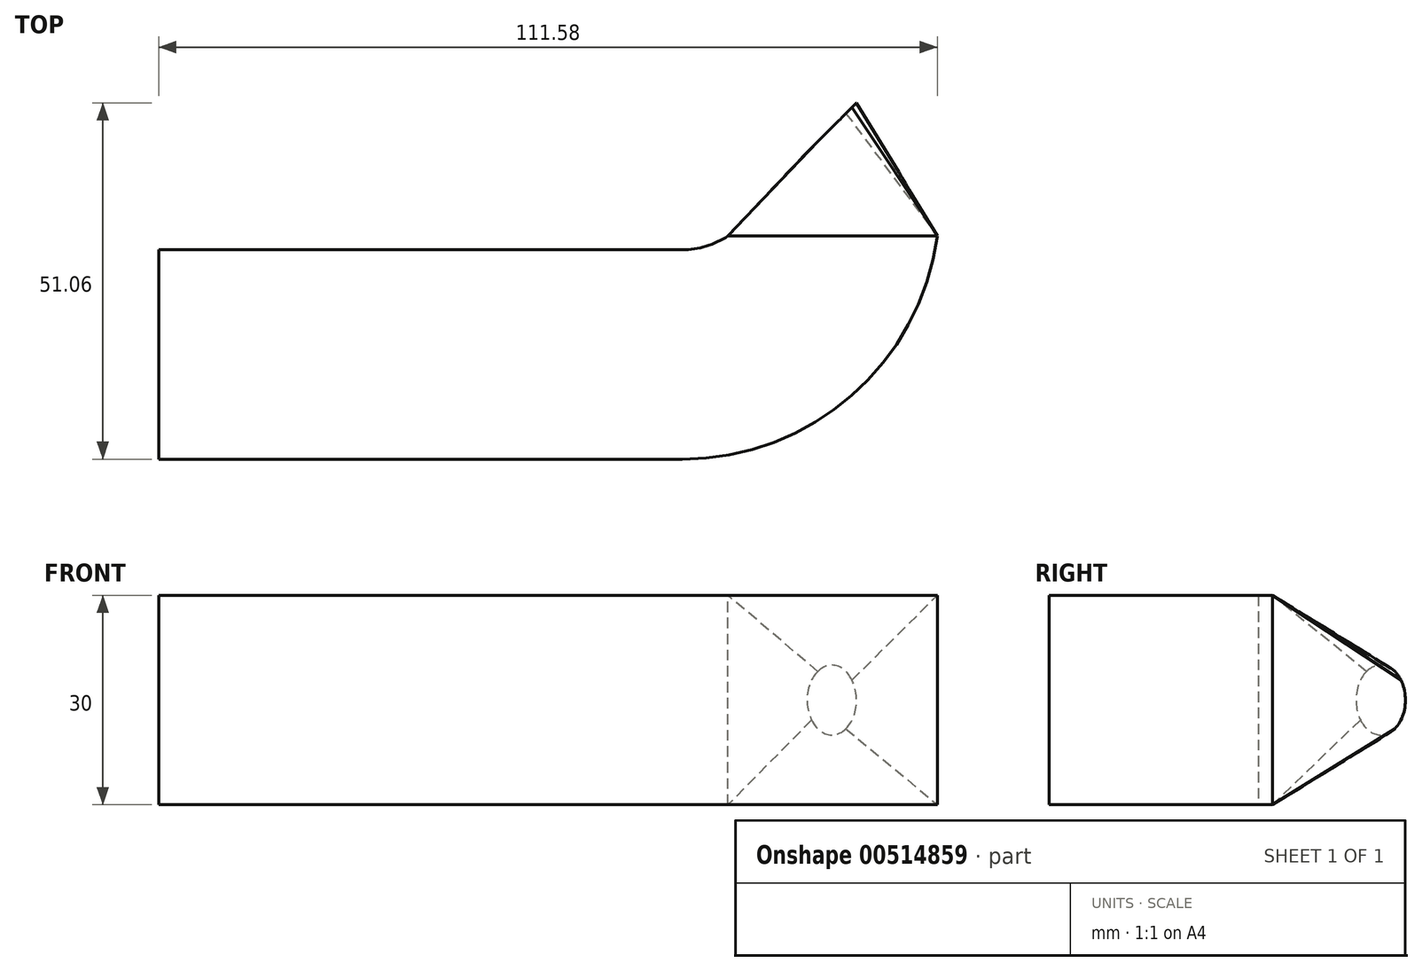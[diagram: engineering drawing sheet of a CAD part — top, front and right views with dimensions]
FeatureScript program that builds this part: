
annotation { "Feature Type Name" : "Feature", "Feature Type Description" : "" }
export const myFeature = defineFeature(function(context is Context, id is Id, definition is map)
    precondition{}
    {
        {
            var Q0;
            Q0=qCreatedBy(makeId("Top.planeOp"),FACE);
            var sketch = newSketch(context, id + "F0", { "sketchPlane" : qUnion([Q0])});
            skLineSegment(sketch, "E0.left", {"start": v(-50, 50) * mm, "end": v(-50, -50) * mm});
            skPoint(sketch, "E0.middle", {"position": v(0, 0) * mm});
            skLineSegment(sketch, "E1", {"start": v(-50, 50) * mm, "end": v(-50, 40) * mm});
            skLineSegment(sketch, "E2", {"start": v(50, 40.02) * mm, "end": v(42.93, 32.95) * mm});
            skPoint(sketch, "E3", {"position": v(-50, 0) * mm});
            skLineSegment(sketch, "E4", {"start": v(42.93, 20.95) * mm, "end": v(46.58, 20.95) * mm});
            skLineSegment(sketch, "E5", {"start": v(42.93, 20.95) * mm, "end": v(-50, 20.95) * mm});
            skLineSegment(sketch, "E6", {"start": v(-50, 40) * mm, "end": v(50, 40.02) * mm});
            skLineSegment(sketch, "E7", {"start": v(-50, 20.95) * mm, "end": v(-50, 18.95) * mm});
            skLineSegment(sketch, "E8", {"start": v(42.93, 20.95) * mm, "end": v(42.93, 32.95) * mm});
            skLineSegment(sketch, "E9", {"start": v(46.46, 36.48) * mm, "end": v(46.58, 20.95) * mm});
            skLineSegment(sketch, "E10", {"start": v(46.58, 20.95) * mm, "end": v(31.58, 20.95) * mm});
            skLineSegment(sketch, "E11", {"start": v(-50, 18.95) * mm, "end": v(25, 18.95) * mm});
            skLineSegment(sketch, "E12", {"start": v(-50, 18.95) * mm, "end": v(-50, 3.95) * mm});
            skSolve(sketch);
        }
        {
            var Q0;
            Q0=sQuery(id+"F0.wireOp",EDGE,"E2");
            cPlane(context, id + "F1", {"entities" : qUnion([Q0]), "cplaneType" : CPlaneType.LINE_ANGLE, "offset" : 25 * mm, "angle" : 90 * degree, "width" : 150 * mm, "height" : 150 * mm});
        }
        {
            var Q0;
            Q0=qCreatedBy(id+"F1.planeOp",FACE);
            var sketch = newSketch(context, id + "F2", { "sketchPlane" : qUnion([Q0])});
            skCircle(sketch, "E13", {"center": v(58.64, 0) * mm, "radius": 5 * mm});
            skSolve(sketch);
        }
        {
            var Q0;
            Q0=qCreatedBy(makeId("Front.planeOp"),FACE);
            var Q1;
            Q1=sQuery(id+"F0.wireOp",VERTEX,"E4.start");
            cPlane(context, id + "F3", {"entities" : qUnion([Q0, Q1]), "cplaneType" : CPlaneType.PLANE_POINT, "offset" : 25 * mm, "width" : 150 * mm, "height" : 150 * mm});
        }
        {
            var Q0;
            Q0=qCreatedBy(id+"F3.planeOp",FACE);
            var sketch = newSketch(context, id + "F4", { "sketchPlane" : qUnion([Q0])});
            skPoint(sketch, "E14", {"position": v(42.93, 0) * mm});
            skPoint(sketch, "E15", {"position": v(46.58, 0) * mm});
            skLineSegment(sketch, "E16.bottom", {"start": v(31.58, -15) * mm, "end": v(61.58, -15) * mm});
            skLineSegment(sketch, "E16.top", {"start": v(31.58, 15) * mm, "end": v(61.58, 15) * mm});
            skLineSegment(sketch, "E16.left", {"start": v(31.58, -15) * mm, "end": v(31.58, 15) * mm});
            skLineSegment(sketch, "E16.right", {"start": v(61.58, -15) * mm, "end": v(61.58, 15) * mm});
            skLineSegment(sketch, "E17", {"start": v(46.58, 0) * mm, "end": v(61.58, 0) * mm});
            skSolve(sketch);
        }
        {
            var Q0;
            Q0=makeQuery(id+"F2.imprint","IMPRINT",FACE,{"disambiguationData":[TD([[makeQuery(id+"F2.imprint","IMPRINT",EDGE,{"derivedFrom":sQuery(id+"F2.wireOp",EDGE,"E13")}),1.0]])]});
            var Q1;
            Q1=makeQuery(id+"F4.imprint","IMPRINT",FACE,{"disambiguationData":[TD([[makeQuery(id+"F4.imprint","IMPRINT",EDGE,{"derivedFrom":sQuery(id+"F4.wireOp",EDGE,"E16.bottom")}),1.0]])]});
            loft(context, id + "F5", {"sheetProfilesArray" : [{ "sheetProfileEntities" : qUnion([Q0]) }, { "sheetProfileEntities" : qUnion([Q1]) }]});
        }
        {
            var Q0;
            Q0=sQuery(id+"F0.wireOp",VERTEX,"E11.end");
            var Q1;
            Q1=qCreatedBy(makeId("Right.planeOp"),FACE);
            cPlane(context, id + "F6", {"entities" : qUnion([Q0, Q1]), "cplaneType" : CPlaneType.PLANE_POINT, "offset" : 25 * mm, "width" : 150 * mm, "height" : 150 * mm});
        }
        {
            var Q0;
            Q0=qCreatedBy(id+"F6.planeOp",FACE);
            var sketch = newSketch(context, id + "F7", { "sketchPlane" : qUnion([Q0])});
            skPoint(sketch, "E18", {"position": v(18.95, 0) * mm});
            skLineSegment(sketch, "E19.bottom", {"start": v(18.95, 15) * mm, "end": v(-11.05, 15) * mm});
            skLineSegment(sketch, "E19.top", {"start": v(18.95, -15) * mm, "end": v(-11.05, -15) * mm});
            skLineSegment(sketch, "E19.left", {"start": v(18.95, 15) * mm, "end": v(18.95, -15) * mm});
            skLineSegment(sketch, "E19.right", {"start": v(-11.05, 15) * mm, "end": v(-11.05, -15) * mm});
            skPoint(sketch, "E19.middle", {"position": v(3.95, 0) * mm});
            skLineSegment(sketch, "E20", {"start": v(3.95, 0) * mm, "end": v(-11.05, 0) * mm});
            skSolve(sketch);
        }
        {
            var Q0;
            Q0=sQuery(id+"F7.wireOp",VERTEX,"E19.middle");
            var Q1;
            Q1=qCreatedBy(makeId("Top.planeOp"),FACE);
            cPlane(context, id + "F8", {"entities" : qUnion([Q0, Q1]), "cplaneType" : CPlaneType.PLANE_POINT, "offset" : 25 * mm, "width" : 150 * mm, "height" : 150 * mm});
        }
        {
            var Q0;
            Q0=qCreatedBy(id+"F8.planeOp",FACE);
            var sketch = newSketch(context, id + "F9", { "sketchPlane" : qUnion([Q0])});
            skPoint(sketch, "E21", {"position": v(25, -11.05) * mm});
            skPoint(sketch, "E22", {"position": v(25, 18.95) * mm});
            skLineSegment(sketch, "E23", {"start": v(25, 18.95) * mm, "end": v(17.07, 18.95) * mm});
            skLineSegment(sketch, "E24", {"start": v(25, -11.05) * mm, "end": v(17.63, -11.05) * mm});
            skPoint(sketch, "E25", {"position": v(31.58, 20.95) * mm});
            skPoint(sketch, "E26", {"position": v(61.58, 20.95) * mm});
            skArc(sketch, "E27", {"start": v(25, 18.95) * mm, "mid": v(28.44, 19.46) * mm, "end": v(31.58, 20.95) * mm});
            skArc(sketch, "E28", {"start": v(25, -11.05) * mm, "mid": v(49.3, -1.92) * mm, "end": v(61.58, 20.95) * mm});
            skLineSegment(sketch, "E29", {"start": v(25, 18.95) * mm, "end": v(25, -11.05) * mm});
            skLineSegment(sketch, "E30", {"start": v(31.58, 20.95) * mm, "end": v(61.58, 20.95) * mm});
            skSolve(sketch);
        }
        {
            var Q0;
            Q0=makeQuery(id+"F9.imprint","IMPRINT",FACE,{"disambiguationData":[TD([[makeQuery(id+"F9.imprint","IMPRINT",EDGE,{"derivedFrom":sQuery(id+"F9.wireOp",EDGE,"E27")}),-1.0]])]});
            extrude(context, id + "F10", {"entities" : qUnion([Q0]), "operationType" : NewBodyOperationType.ADD, "endBound" : BoundingType.SYMMETRIC, "depth" : 30 * mm, "offsetDistance" : 25 * mm});
        }
        {
            var Q0;
            Q0=qCreatedBy(makeId("Top.planeOp"),FACE);
            var sketch = newSketch(context, id + "F11", { "sketchPlane" : qUnion([Q0])});
            skPoint(sketch, "E31", {"position": v(25, 3.95) * mm});
            skPoint(sketch, "E32", {"position": v(-50, 3.95) * mm});
            skLineSegment(sketch, "E33", {"start": v(-50, 3.95) * mm, "end": v(25, 3.95) * mm});
            skSolve(sketch);
        }
        {
            var Q0;
            {var subQ1=sQuery(id+"F7.wireOp",EDGE,"E19.bottom");Q0=makeQuery(id+"F7.imprint","IMPRINT",FACE,{"disambiguationData":[TD([[makeQuery(id+"F7.imprint","IMPRINT",EDGE,{"derivedFrom":subQ1}),1.0]])]});}
            var Q1;
            Q1=sQuery(id+"F11.wireOp",EDGE,"E33");
            sweep(context, id + "F12", {"operationType" : NewBodyOperationType.ADD, "profiles" : qUnion([Q0]), "path" : qUnion([Q1])});
        }
    });
